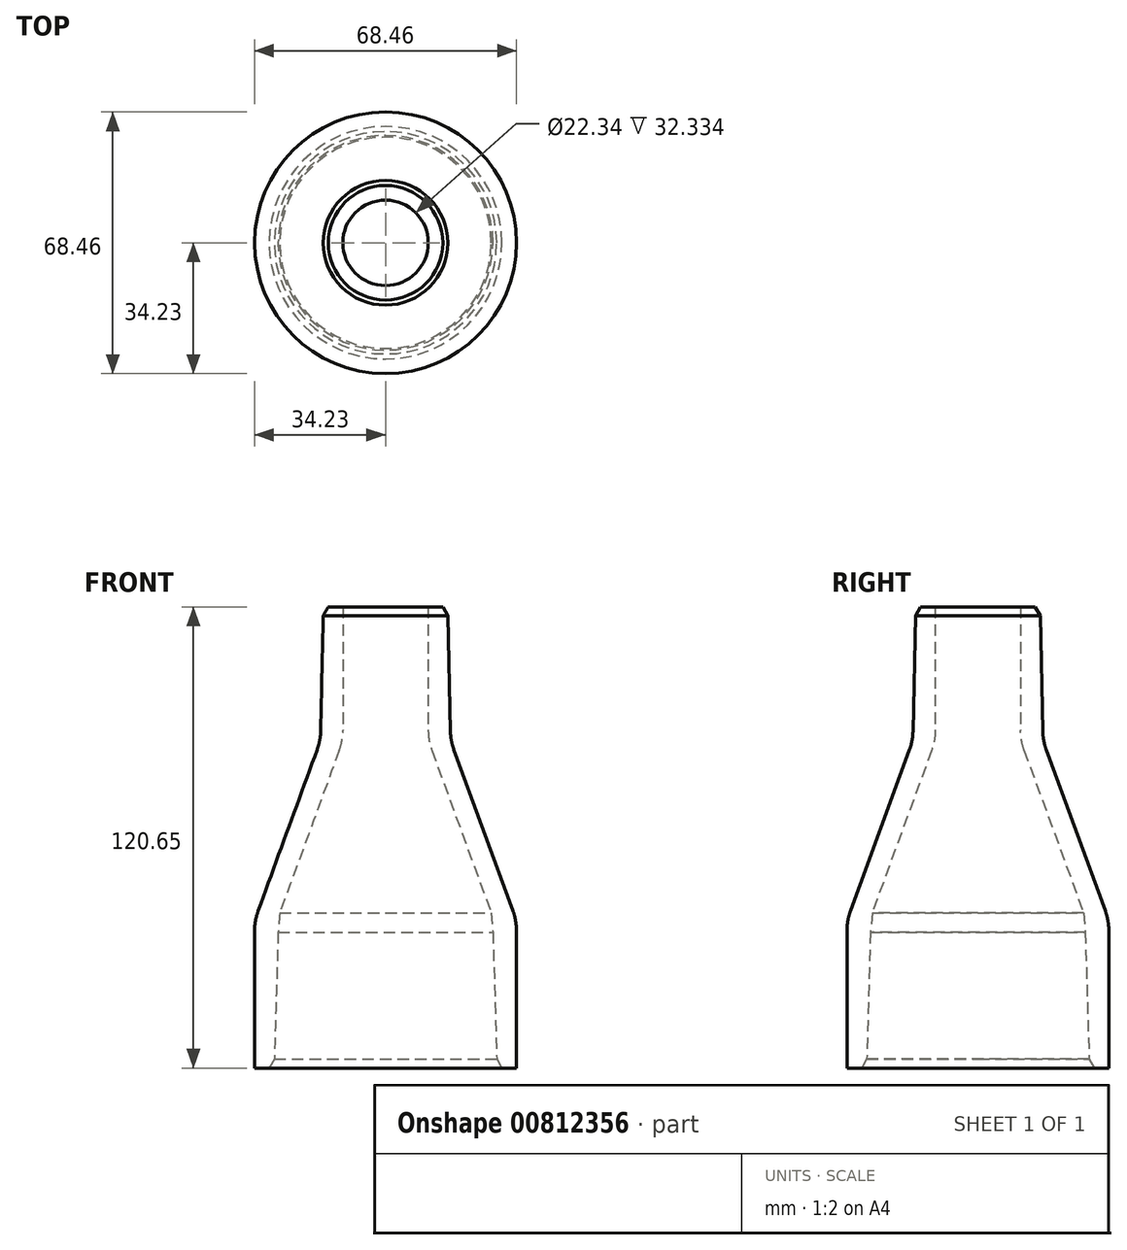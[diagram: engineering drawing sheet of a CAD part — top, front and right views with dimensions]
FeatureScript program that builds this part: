
annotation { "Feature Type Name" : "Feature", "Feature Type Description" : "" }
export const myFeature = defineFeature(function(context is Context, id is Id, definition is map)
    precondition{}
    {
        {
            var Q0;
            Q0=qCreatedBy(makeId("Front.planeOp"),FACE);
            var sketch = newSketch(context, id + "F0", { "sketchPlane" : qUnion([Q0])});
            skLineSegment(sketch, "E0", {"start": v(0, 0) * mm, "end": v(0, 169.36) * mm});
            skLineSegment(sketch, "E1", {"start": v(-29.15, 0) * mm, "end": v(-34.23, 0) * mm});
            skLineSegment(sketch, "E2", {"start": v(-29.15, 0) * mm, "end": v(-28.08, 35.56) * mm});
            skPoint(sketch, "E3", {"position": v(-28.6, 18.29) * mm});
            skLineSegment(sketch, "E4", {"start": v(-28.08, 35.56) * mm, "end": v(-27.64, 40.64) * mm});
            skPoint(sketch, "E5.orphan", {"position": v(-27.93, 40.64) * mm});
            skLineSegment(sketch, "E6", {"start": v(-34.23, 0) * mm, "end": v(-34.23, 38.62) * mm});
            skLineSegment(sketch, "E7", {"start": v(-34.23, 38.62) * mm, "end": v(-17.02, 85.66) * mm});
            skLineSegment(sketch, "E8", {"start": v(-17.02, 85.66) * mm, "end": v(-16.25, 120.65) * mm});
            skLineSegment(sketch, "E9", {"start": v(-27.64, 40.64) * mm, "end": v(-11.17, 85.66) * mm});
            skLineSegment(sketch, "E10", {"start": v(-11.17, 85.66) * mm, "end": v(-11.17, 120.65) * mm});
            skLineSegment(sketch, "E11", {"start": v(-11.17, 120.65) * mm, "end": v(-16.25, 120.65) * mm});
            skLineSegment(sketch, "E12", {"start": v(-29.08, 2.32) * mm, "end": v(-30.42, 0) * mm});
            skLineSegment(sketch, "E13", {"start": v(-14.98, 120.65) * mm, "end": v(-16.3, 118.36) * mm});
            skSolve(sketch);
        }
        {
            var Q0;
            {var subQ8=sQuery(id+"F0.wireOp",EDGE,"E4");Q0=makeQuery(id+"F0.imprint","IMPRINT",FACE,{"disambiguationData":[TD([[makeQuery(id+"F0.imprint","IMPRINT",EDGE,{"derivedFrom":subQ8}),1.0]])]});}
            var Q1;
            Q1=sQuery(id+"F0.wireOp",EDGE,"E0");
            revolve(context, id + "F1", {"surfaceOperationType" : NewSurfaceOperationType.NEW, "entities" : qUnion([Q0]), "axis" : qUnion([Q1]), "revolveType" : RevolveType.FULL});
        }
        {
            var Q0;
            Q0=makeQuery(id+"F1.opRevolve","SWEPT_EDGE",EDGE,{"disambiguationData":[OSD([sQuery(id+"F0.wireOp",EDGE,"E6"),sQuery(id+"F0.wireOp",EDGE,"E7")])]});
            var Q1;
            Q1=makeQuery(id+"F1.opRevolve","SWEPT_EDGE",EDGE,{"disambiguationData":[OSD([sQuery(id+"F0.wireOp",EDGE,"E7"),sQuery(id+"F0.wireOp",EDGE,"E8")])]});
            var Q2;
            Q2=makeQuery(id+"F1.opRevolve","SWEPT_EDGE",EDGE,{"disambiguationData":[OSD([sQuery(id+"F0.wireOp",EDGE,"E9"),sQuery(id+"F0.wireOp",EDGE,"E10")])]});
            fillet(context, id + "F2", {"entities" : qUnion([Q0, Q1, Q2]), "tangentPropagation" : true, "radius" : 15 * mm, "defaultsChanged" : false, "vertexSettings" : [], "allowEdgeOverflow" : false});
        }
    });
